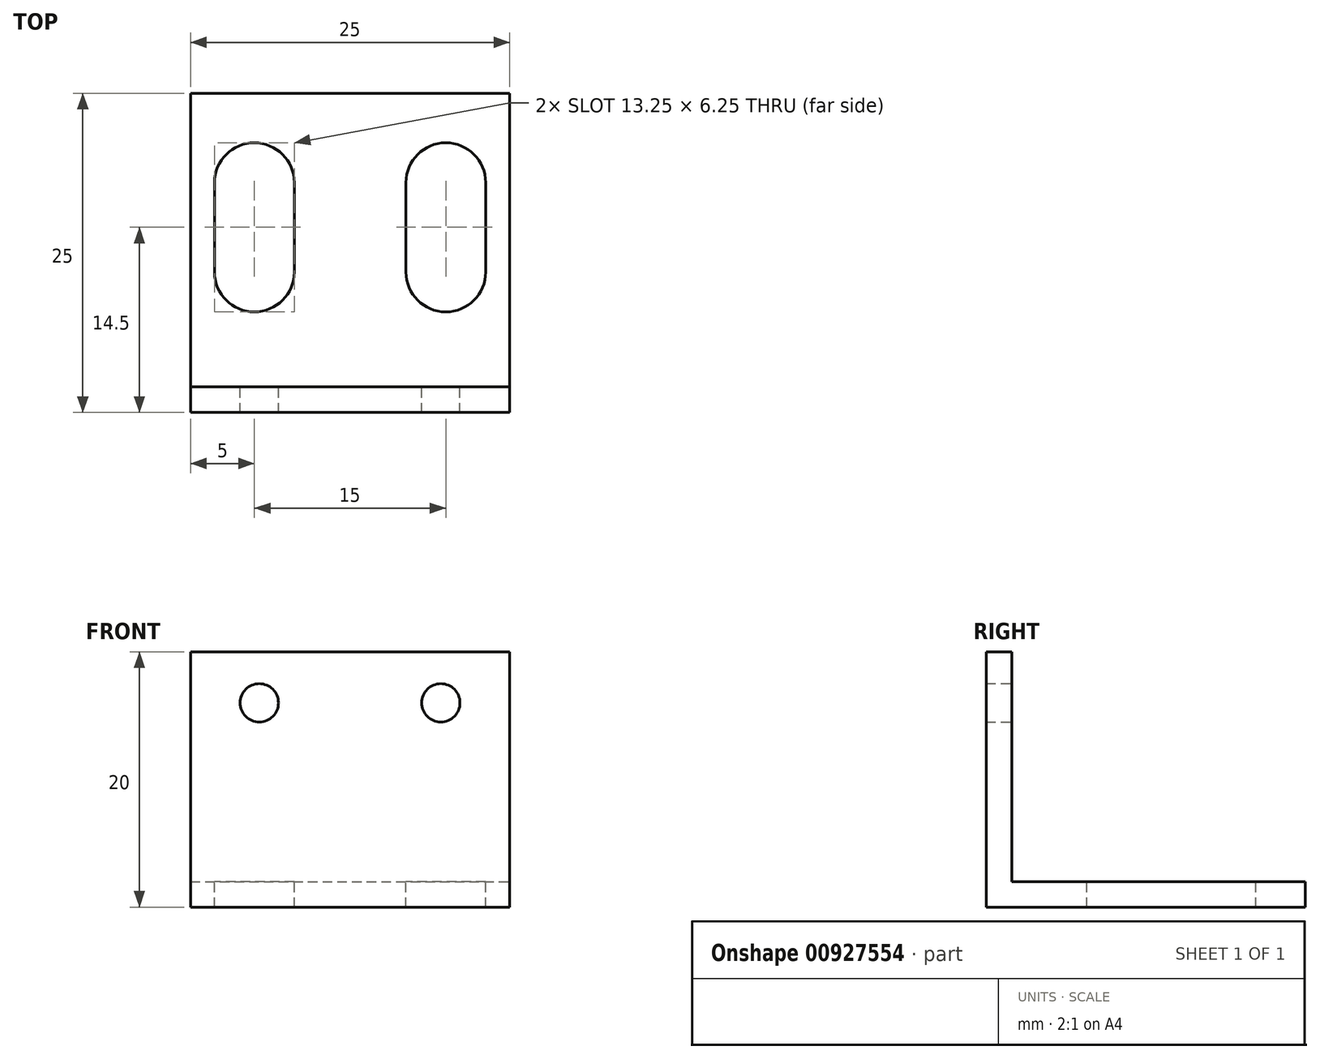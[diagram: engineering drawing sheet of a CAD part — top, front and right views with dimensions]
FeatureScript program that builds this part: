
annotation { "Feature Type Name" : "Feature", "Feature Type Description" : "" }
export const myFeature = defineFeature(function(context is Context, id is Id, definition is map)
    precondition{}
    {
        {
            var Q0;
            Q0=qCreatedBy(makeId("Right.planeOp"),FACE);
            var sketch = newSketch(context, id + "F0", { "sketchPlane" : qUnion([Q0])});
            skLineSegment(sketch, "E0", {"start": v(0, 0) * mm, "end": v(-25, 0) * mm});
            skLineSegment(sketch, "E1", {"start": v(-25, 0) * mm, "end": v(-25, 20) * mm});
            skLineSegment(sketch, "E2.0", {"start": v(-23, 2) * mm, "end": v(-23, 20) * mm});
            skLineSegment(sketch, "E2.1", {"start": v(0, 2) * mm, "end": v(-23, 2) * mm});
            skLineSegment(sketch, "E3", {"start": v(-25, 20) * mm, "end": v(-23, 20) * mm});
            skLineSegment(sketch, "E4", {"start": v(0, 2) * mm, "end": v(0, 0) * mm});
            skSolve(sketch);
        }
        {
            var Q0;
            Q0 = qSketchRegion(id + "F0", true);
            extrude(context, id + "F1", {"entities" : qUnion([Q0]), "oppositeDirection" : true, "depth" : 25 * mm, "offsetDistance" : 25 * mm});
        }
        {
            var Q0;
            Q0=makeQuery(id+"F1.opExtrude","SWEPT_FACE",FACE,{"disambiguationData":[OSD([sQuery(id+"F0.wireOp",EDGE,"E2.1")])]});
            var sketch = newSketch(context, id + "F2", { "sketchPlane" : qUnion([Q0])});
            skArc(sketch, "E5", {"start": v(-16.88, -7) * mm, "mid": v(-20, -3.88) * mm, "end": v(-23.12, -7) * mm});
            skArc(sketch, "E6", {"start": v(-1.88, -7) * mm, "mid": v(-5, -3.87) * mm, "end": v(-8.12, -7) * mm});
            skArc(sketch, "E7", {"start": v(-8.12, -14) * mm, "mid": v(-5, -17.12) * mm, "end": v(-1.88, -14) * mm});
            skLineSegment(sketch, "E8", {"start": v(-23.12, -7) * mm, "end": v(-23.12, -14) * mm});
            skLineSegment(sketch, "E9", {"start": v(-16.88, -7) * mm, "end": v(-16.88, -14) * mm});
            skLineSegment(sketch, "E10", {"start": v(-8.12, -7) * mm, "end": v(-8.12, -14) * mm});
            skLineSegment(sketch, "E11", {"start": v(-1.88, -7) * mm, "end": v(-1.88, -14) * mm});
            skArc(sketch, "E12.trimOffspring", {"start": v(-23.12, -14) * mm, "mid": v(-20, -17.12) * mm, "end": v(-16.88, -14) * mm});
            skSolve(sketch);
        }
        {
            var Q0;
            Q0 = qSketchRegion(id + "F2", true);
            extrude(context, id + "F3", {"entities" : qUnion([Q0]), "operationType" : NewBodyOperationType.REMOVE, "oppositeDirection" : true, "depth" : 25 * mm, "offsetDistance" : 25 * mm});
        }
        {
            var Q0;
            Q0=makeQuery(id+"F1.opExtrude","SWEPT_FACE",FACE,{"disambiguationData":[OSD([sQuery(id+"F0.wireOp",EDGE,"E2.0")])]});
            var sketch = newSketch(context, id + "F4", { "sketchPlane" : qUnion([Q0])});
            skCircle(sketch, "E13", {"center": v(5.39, 16) * mm, "radius": 1.5 * mm});
            skCircle(sketch, "E14", {"center": v(19.61, 16) * mm, "radius": 1.5 * mm});
            skPoint(sketch, "E15", {"position": v(12.5, 20) * mm});
            skSolve(sketch);
        }
        {
            var Q0;
            Q0=makeQuery(id+"F4.imprint","IMPRINT",FACE,{"disambiguationData":[TD([[makeQuery(id+"F4.imprint","IMPRINT",EDGE,{"derivedFrom":sQuery(id+"F4.wireOp",EDGE,"E13")}),1.0]])]});
            var Q1;
            Q1=makeQuery(id+"F4.imprint","IMPRINT",FACE,{"disambiguationData":[TD([[makeQuery(id+"F4.imprint","IMPRINT",EDGE,{"derivedFrom":sQuery(id+"F4.wireOp",EDGE,"E14")}),1.0]])]});
            extrude(context, id + "F5", {"entities" : qUnion([Q0, Q1]), "operationType" : NewBodyOperationType.REMOVE, "oppositeDirection" : true, "depth" : 25 * mm, "offsetDistance" : 25 * mm});
        }
    });
